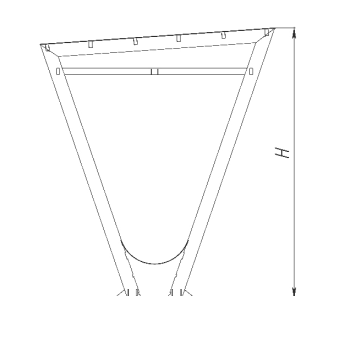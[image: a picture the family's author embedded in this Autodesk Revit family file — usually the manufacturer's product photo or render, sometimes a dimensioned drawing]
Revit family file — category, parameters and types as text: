
# Revit family: Пергола-качели «Релакс» Арт 14128 L10540
name_source: partatom
category: Антураж
revit_build: Autodesk Revit 2018 (Build: 20180423_1000(x64)
units: mm (PartAtom-declared; Revit-internal decimal feet)

## family parameters
Всегда вертикально = Да
Источник визуального образа = Геометрия семейства
На основе рабочей плоскости = Нет
Общий = Нет
При загрузке вырезать с полостями = Нет
Точка расчета площади = Нет

## types (1)
- L10540
    Rv = 9074 мм
    URL = https://hobbyka.ru
    Артикул товара = Арт. 14128
    Высота = 3300 мм
    Группа модели = Парковые качели
    Длина = 10540 мм
    Изготовитель = ООО «Хоббика»
    Изображение типоразмера = Пергола-качели «Релакс» Арт 14128.jpg
    Материал изделия = Сталь, дерево, поликарбонат
    Материал крыши = Поликарбанат корич
    Описание = Пергола-качели «Релакс» L10540
    Радиус внешний = 11954 мм
    Угол = 50.52°
    Угол 1/3 = 16.84°
    Угол 2/3 = 33.68°
    Угол качель 1 = 9.34°
    Угол качель 2 = 27.05°
    Угол качель 3 = 44.64°
    Цвет каркаса = Сталь
    Цвет качели = Дерево Тик
    Ширина = 2880 мм
